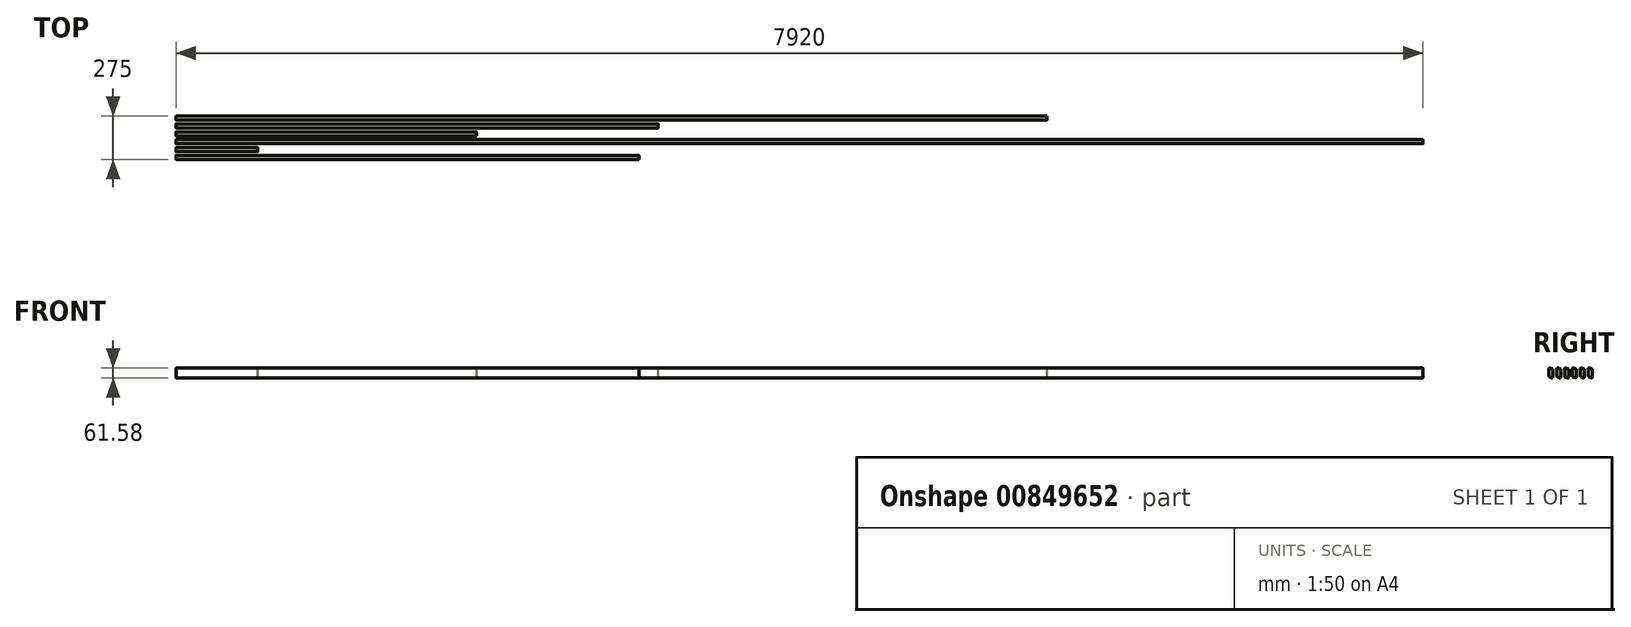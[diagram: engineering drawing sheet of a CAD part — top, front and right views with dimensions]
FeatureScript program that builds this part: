
annotation { "Feature Type Name" : "Feature", "Feature Type Description" : "" }
export const myFeature = defineFeature(function(context is Context, id is Id, definition is map)
    precondition{}
    {
        {
            var Q0;
            Q0=qCreatedBy(makeId("Right.planeOp"),FACE);
            var sketch = newSketch(context, id + "F0", { "sketchPlane" : qUnion([Q0])});
            skLineSegment(sketch, "E0", {"start": v(0, 5.71) * mm, "end": v(0, 53.1) * mm});
            skLineSegment(sketch, "E1", {"start": v(-2.63, 56.86) * mm, "end": v(-19.63, 63.05) * mm});
            skLineSegment(sketch, "E2", {"start": v(-25, 59.29) * mm, "end": v(-25, 11.9) * mm});
            skLineSegment(sketch, "E3", {"start": v(-22.37, 8.14) * mm, "end": v(-5.37, 1.95) * mm});
            skPoint(sketch, "E4.visualSharp", {"position": v(-25, 65) * mm});
            skArc(sketch, "E4.filletArc", {"start": v(-19.63, 63.05) * mm, "mid": v(-23.3, 62.56) * mm, "end": v(-25, 59.29) * mm});
            skPoint(sketch, "E5.visualSharp", {"position": v(-25, 9.1) * mm});
            skArc(sketch, "E5.filletArc", {"start": v(-25, 11.9) * mm, "mid": v(-24.28, 9.6) * mm, "end": v(-22.37, 8.14) * mm});
            skPoint(sketch, "E6.visualSharp", {"position": v(0, 0) * mm});
            skArc(sketch, "E6.filletArc", {"start": v(-5.37, 1.95) * mm, "mid": v(-1.7, 2.44) * mm, "end": v(0, 5.71) * mm});
            skPoint(sketch, "E7.visualSharp", {"position": v(0, 55.9) * mm});
            skArc(sketch, "E7.filletArc", {"start": v(0, 53.1) * mm, "mid": v(-0.72, 55.4) * mm, "end": v(-2.63, 56.86) * mm});
            skLineSegment(sketch, "E8.1.0.0", {"start": v(-75, 59.29) * mm, "end": v(-75, 11.9) * mm});
            skLineSegment(sketch, "E8.1.0.1", {"start": v(-52.63, 56.86) * mm, "end": v(-69.63, 63.05) * mm});
            skArc(sketch, "E8.1.0.2", {"start": v(-69.63, 63.05) * mm, "mid": v(-73.3, 62.56) * mm, "end": v(-75, 59.29) * mm});
            skLineSegment(sketch, "E8.1.0.3", {"start": v(-50, 5.71) * mm, "end": v(-50, 53.1) * mm});
            skLineSegment(sketch, "E8.1.0.4", {"start": v(-72.37, 8.14) * mm, "end": v(-55.37, 1.95) * mm});
            skArc(sketch, "E8.1.0.5", {"start": v(-55.37, 1.95) * mm, "mid": v(-51.7, 2.44) * mm, "end": v(-50, 5.71) * mm});
            skArc(sketch, "E8.1.0.6", {"start": v(-75, 11.9) * mm, "mid": v(-74.28, 9.6) * mm, "end": v(-72.37, 8.14) * mm});
            skArc(sketch, "E8.1.0.7", {"start": v(-50, 53.1) * mm, "mid": v(-50.72, 55.4) * mm, "end": v(-52.63, 56.86) * mm});
            skLineSegment(sketch, "E8.2.0.0", {"start": v(-125, 59.29) * mm, "end": v(-125, 11.9) * mm});
            skLineSegment(sketch, "E8.2.0.1", {"start": v(-102.63, 56.86) * mm, "end": v(-119.63, 63.05) * mm});
            skArc(sketch, "E8.2.0.2", {"start": v(-119.63, 63.05) * mm, "mid": v(-123.3, 62.56) * mm, "end": v(-125, 59.29) * mm});
            skLineSegment(sketch, "E8.2.0.3", {"start": v(-100, 5.71) * mm, "end": v(-100, 53.1) * mm});
            skLineSegment(sketch, "E8.2.0.4", {"start": v(-122.37, 8.14) * mm, "end": v(-105.37, 1.95) * mm});
            skArc(sketch, "E8.2.0.5", {"start": v(-105.37, 1.95) * mm, "mid": v(-101.7, 2.44) * mm, "end": v(-100, 5.71) * mm});
            skArc(sketch, "E8.2.0.6", {"start": v(-125, 11.9) * mm, "mid": v(-124.28, 9.6) * mm, "end": v(-122.37, 8.14) * mm});
            skArc(sketch, "E8.2.0.7", {"start": v(-100, 53.1) * mm, "mid": v(-100.72, 55.4) * mm, "end": v(-102.63, 56.86) * mm});
            skLineSegment(sketch, "E8.3.0.0", {"start": v(-175, 59.29) * mm, "end": v(-175, 11.9) * mm});
            skLineSegment(sketch, "E8.3.0.1", {"start": v(-152.63, 56.86) * mm, "end": v(-169.63, 63.05) * mm});
            skArc(sketch, "E8.3.0.2", {"start": v(-169.63, 63.05) * mm, "mid": v(-173.3, 62.56) * mm, "end": v(-175, 59.29) * mm});
            skLineSegment(sketch, "E8.3.0.3", {"start": v(-150, 5.71) * mm, "end": v(-150, 53.1) * mm});
            skLineSegment(sketch, "E8.3.0.4", {"start": v(-172.37, 8.14) * mm, "end": v(-155.37, 1.95) * mm});
            skArc(sketch, "E8.3.0.5", {"start": v(-155.37, 1.95) * mm, "mid": v(-151.7, 2.44) * mm, "end": v(-150, 5.71) * mm});
            skArc(sketch, "E8.3.0.6", {"start": v(-175, 11.9) * mm, "mid": v(-174.28, 9.6) * mm, "end": v(-172.37, 8.14) * mm});
            skArc(sketch, "E8.3.0.7", {"start": v(-150, 53.1) * mm, "mid": v(-150.72, 55.4) * mm, "end": v(-152.63, 56.86) * mm});
            skLineSegment(sketch, "E8.4.0.0", {"start": v(-225, 59.29) * mm, "end": v(-225, 11.9) * mm});
            skLineSegment(sketch, "E8.4.0.1", {"start": v(-202.63, 56.86) * mm, "end": v(-219.63, 63.05) * mm});
            skArc(sketch, "E8.4.0.2", {"start": v(-219.63, 63.05) * mm, "mid": v(-223.3, 62.56) * mm, "end": v(-225, 59.29) * mm});
            skLineSegment(sketch, "E8.4.0.3", {"start": v(-200, 5.71) * mm, "end": v(-200, 53.1) * mm});
            skLineSegment(sketch, "E8.4.0.4", {"start": v(-222.37, 8.14) * mm, "end": v(-205.37, 1.95) * mm});
            skArc(sketch, "E8.4.0.5", {"start": v(-205.37, 1.95) * mm, "mid": v(-201.7, 2.44) * mm, "end": v(-200, 5.71) * mm});
            skArc(sketch, "E8.4.0.6", {"start": v(-225, 11.9) * mm, "mid": v(-224.28, 9.6) * mm, "end": v(-222.37, 8.14) * mm});
            skArc(sketch, "E8.4.0.7", {"start": v(-200, 53.1) * mm, "mid": v(-200.72, 55.4) * mm, "end": v(-202.63, 56.86) * mm});
            skLineSegment(sketch, "E8.5.0.0", {"start": v(-275, 59.29) * mm, "end": v(-275, 11.9) * mm});
            skLineSegment(sketch, "E8.5.0.1", {"start": v(-252.63, 56.86) * mm, "end": v(-269.63, 63.05) * mm});
            skArc(sketch, "E8.5.0.2", {"start": v(-269.63, 63.05) * mm, "mid": v(-273.3, 62.56) * mm, "end": v(-275, 59.29) * mm});
            skLineSegment(sketch, "E8.5.0.3", {"start": v(-250, 5.71) * mm, "end": v(-250, 53.1) * mm});
            skLineSegment(sketch, "E8.5.0.4", {"start": v(-272.37, 8.14) * mm, "end": v(-255.37, 1.95) * mm});
            skArc(sketch, "E8.5.0.5", {"start": v(-255.37, 1.95) * mm, "mid": v(-251.7, 2.44) * mm, "end": v(-250, 5.71) * mm});
            skArc(sketch, "E8.5.0.6", {"start": v(-275, 11.9) * mm, "mid": v(-274.28, 9.6) * mm, "end": v(-272.37, 8.14) * mm});
            skArc(sketch, "E8.5.0.7", {"start": v(-250, 53.1) * mm, "mid": v(-250.72, 55.4) * mm, "end": v(-252.63, 56.86) * mm});
            skLineSegment(sketch, "E8.6.0.0", {"start": v(-325, 59.29) * mm, "end": v(-325, 11.9) * mm});
            skLineSegment(sketch, "E8.6.0.1", {"start": v(-302.63, 56.86) * mm, "end": v(-319.63, 63.05) * mm});
            skArc(sketch, "E8.6.0.2", {"start": v(-319.63, 63.05) * mm, "mid": v(-323.3, 62.56) * mm, "end": v(-325, 59.29) * mm});
            skLineSegment(sketch, "E8.6.0.3", {"start": v(-300, 5.71) * mm, "end": v(-300, 53.1) * mm});
            skLineSegment(sketch, "E8.6.0.4", {"start": v(-322.37, 8.14) * mm, "end": v(-305.37, 1.95) * mm});
            skArc(sketch, "E8.6.0.5", {"start": v(-305.37, 1.95) * mm, "mid": v(-301.7, 2.44) * mm, "end": v(-300, 5.71) * mm});
            skArc(sketch, "E8.6.0.6", {"start": v(-325, 11.9) * mm, "mid": v(-324.28, 9.6) * mm, "end": v(-322.37, 8.14) * mm});
            skArc(sketch, "E8.6.0.7", {"start": v(-300, 53.1) * mm, "mid": v(-300.72, 55.4) * mm, "end": v(-302.63, 56.86) * mm});
            skLineSegment(sketch, "E8.7.0.0", {"start": v(-375, 59.29) * mm, "end": v(-375, 11.9) * mm});
            skLineSegment(sketch, "E8.7.0.1", {"start": v(-352.63, 56.86) * mm, "end": v(-369.63, 63.05) * mm});
            skArc(sketch, "E8.7.0.2", {"start": v(-369.63, 63.05) * mm, "mid": v(-373.3, 62.56) * mm, "end": v(-375, 59.29) * mm});
            skLineSegment(sketch, "E8.7.0.3", {"start": v(-350, 5.71) * mm, "end": v(-350, 53.1) * mm});
            skLineSegment(sketch, "E8.7.0.4", {"start": v(-372.37, 8.14) * mm, "end": v(-355.37, 1.95) * mm});
            skArc(sketch, "E8.7.0.5", {"start": v(-355.37, 1.95) * mm, "mid": v(-351.7, 2.44) * mm, "end": v(-350, 5.71) * mm});
            skArc(sketch, "E8.7.0.6", {"start": v(-375, 11.9) * mm, "mid": v(-374.28, 9.6) * mm, "end": v(-372.37, 8.14) * mm});
            skArc(sketch, "E8.7.0.7", {"start": v(-350, 53.1) * mm, "mid": v(-350.72, 55.4) * mm, "end": v(-352.63, 56.86) * mm});
            skLineSegment(sketch, "E8.8.0.0", {"start": v(-425, 59.29) * mm, "end": v(-425, 11.9) * mm});
            skLineSegment(sketch, "E8.8.0.1", {"start": v(-402.63, 56.86) * mm, "end": v(-419.63, 63.05) * mm});
            skArc(sketch, "E8.8.0.2", {"start": v(-419.63, 63.05) * mm, "mid": v(-423.3, 62.56) * mm, "end": v(-425, 59.29) * mm});
            skLineSegment(sketch, "E8.8.0.3", {"start": v(-400, 5.71) * mm, "end": v(-400, 53.1) * mm});
            skLineSegment(sketch, "E8.8.0.4", {"start": v(-422.37, 8.14) * mm, "end": v(-405.37, 1.95) * mm});
            skArc(sketch, "E8.8.0.5", {"start": v(-405.37, 1.95) * mm, "mid": v(-401.7, 2.44) * mm, "end": v(-400, 5.71) * mm});
            skArc(sketch, "E8.8.0.6", {"start": v(-425, 11.9) * mm, "mid": v(-424.28, 9.6) * mm, "end": v(-422.37, 8.14) * mm});
            skArc(sketch, "E8.8.0.7", {"start": v(-400, 53.1) * mm, "mid": v(-400.72, 55.4) * mm, "end": v(-402.63, 56.86) * mm});
            skLineSegment(sketch, "E8.9.0.0", {"start": v(-475, 59.29) * mm, "end": v(-475, 11.9) * mm});
            skLineSegment(sketch, "E8.9.0.1", {"start": v(-452.63, 56.86) * mm, "end": v(-469.63, 63.05) * mm});
            skArc(sketch, "E8.9.0.2", {"start": v(-469.63, 63.05) * mm, "mid": v(-473.3, 62.56) * mm, "end": v(-475, 59.29) * mm});
            skLineSegment(sketch, "E8.9.0.3", {"start": v(-450, 5.71) * mm, "end": v(-450, 53.1) * mm});
            skLineSegment(sketch, "E8.9.0.4", {"start": v(-472.37, 8.14) * mm, "end": v(-455.37, 1.95) * mm});
            skArc(sketch, "E8.9.0.5", {"start": v(-455.37, 1.95) * mm, "mid": v(-451.7, 2.44) * mm, "end": v(-450, 5.71) * mm});
            skArc(sketch, "E8.9.0.6", {"start": v(-475, 11.9) * mm, "mid": v(-474.28, 9.6) * mm, "end": v(-472.37, 8.14) * mm});
            skArc(sketch, "E8.9.0.7", {"start": v(-450, 53.1) * mm, "mid": v(-450.72, 55.4) * mm, "end": v(-452.63, 56.86) * mm});
            skLineSegment(sketch, "E8.direction1", {"start": v(-25, 11.9) * mm, "end": v(-75, 11.9) * mm, "construction": true});
            skSolve(sketch);
        }
        {
            var Q0;
            Q0=makeQuery(id+"F0.imprint","IMPRINT",FACE,{"disambiguationData":[TD([[makeQuery(id+"F0.imprint","IMPRINT",EDGE,{"derivedFrom":sQuery(id+"F0.wireOp",EDGE,"E0")}),1.0]])]});
            extrude(context, id + "F1", {"entities" : qUnion([Q0]), "depth" : 5531 * mm, "offsetDistance" : 25 * mm});
        }
        {
            var Q0;
            Q0=makeQuery(id+"F0.imprint","IMPRINT",FACE,{"disambiguationData":[TD([[makeQuery(id+"F0.imprint","IMPRINT",EDGE,{"derivedFrom":sQuery(id+"F0.wireOp",EDGE,"E8.1.0.0")}),1.0]])]});
            extrude(context, id + "F2", {"entities" : qUnion([Q0]), "depth" : 3063 * mm, "offsetDistance" : 25 * mm});
        }
        {
            var Q0;
            Q0=makeQuery(id+"F0.imprint","IMPRINT",FACE,{"disambiguationData":[TD([[makeQuery(id+"F0.imprint","IMPRINT",EDGE,{"derivedFrom":sQuery(id+"F0.wireOp",EDGE,"E8.2.0.0")}),1.0]])]});
            extrude(context, id + "F3", {"entities" : qUnion([Q0]), "depth" : 1908 * mm, "offsetDistance" : 25 * mm});
        }
        {
            var Q0;
            Q0=makeQuery(id+"F0.imprint","IMPRINT",FACE,{"disambiguationData":[TD([[makeQuery(id+"F0.imprint","IMPRINT",EDGE,{"derivedFrom":sQuery(id+"F0.wireOp",EDGE,"E8.3.0.0")}),1.0]])]});
            extrude(context, id + "F4", {"entities" : qUnion([Q0]), "depth" : 7920 * mm, "offsetDistance" : 25 * mm});
        }
        {
            var Q0;
            Q0=makeQuery(id+"F0.imprint","IMPRINT",FACE,{"disambiguationData":[TD([[makeQuery(id+"F0.imprint","IMPRINT",EDGE,{"derivedFrom":sQuery(id+"F0.wireOp",EDGE,"E8.4.0.0")}),1.0]])]});
            extrude(context, id + "F5", {"entities" : qUnion([Q0]), "depth" : 520 * mm, "offsetDistance" : 25 * mm});
        }
        {
            var Q0;
            Q0=makeQuery(id+"F0.imprint","IMPRINT",FACE,{"disambiguationData":[TD([[makeQuery(id+"F0.imprint","IMPRINT",EDGE,{"derivedFrom":sQuery(id+"F0.wireOp",EDGE,"E8.5.0.0")}),1.0]])]});
            extrude(context, id + "F6", {"entities" : qUnion([Q0]), "depth" : 2940 * mm, "offsetDistance" : 25 * mm});
        }
    });
